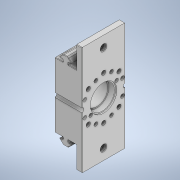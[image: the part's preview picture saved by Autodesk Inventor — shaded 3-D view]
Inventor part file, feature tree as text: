
AUTODESK INVENTOR PART (.ipt)
format: ipt  version: 2020 (Build 240168000, 168)  size: 503,808 bytes
history: native  units: in
note: dims shown in document units (in); Inventor stores cm internally (conversion verified against a paired STEP export)
features: reference x24, extrude x11, sketch x9, other x4, chamfer x2, fillet x1
ambient origin geometry x8: Origin, YZ Plane, XZ Plane, XY Plane, X Axis, Y Axis, Z Axis, Center Point
bodies: Solid1 (feature_tree)
feature tree (51):
  extrude  "Extrusion1"  Depth=5.0in
  extrude  "Extrusion2"  Depth=2.0in TaperAngle=0.0deg
  extrude  "Extrusion4"  Depth=0.5in
  extrude  "Extrusion5"  Depth=0.7874in
  extrude  "Extrusion6"  Depth=2.5in
  extrude  "Extrusion7"  Depth=1.023in
  extrude  "Extrusion8"  Depth=0.314in TaperAngle=0.0deg
  chamfer  "Chamfer3"  Distance=0.064in
  extrude  "Extrusion9"  Depth=0.025in TaperAngle=0.0deg
  extrude  "Extrusion10"  Depth=0.025in
  extrude  "Extrusion11"  Depth=0.025in TaperAngle=0.0deg
  extrude  "Extrusion12"  Depth=0.025in
  fillet  "Fillet1"  Radius=0.165in
  chamfer  "Chamfer4"  [1 undecoded]
  sketch  "Sketch1"  dims[d0=1.25in d1=5.0in]
  reference  "Reference1"
  reference  "Reference2"
  reference  "Reference3"
  reference  "Reference4"
  reference  "Reference5"
  reference  "Reference6"
  reference  "Reference7"
  reference  "Reference8"
  reference  "Reference9"
  reference  "Reference10"
  reference  "Reference11"
  reference  "Reference12"
  reference  "Reference13"
  reference  "Reference14"
  reference  "Reference15"
  reference  "Reference16"
  reference  "Reference17"
  reference  "Reference18"
  reference  "Reference19"
  reference  "Reference20"
  reference  "Reference21"
  reference  "Reference22"
  reference  "Reference23"
  reference  "Reference24"
  sketch  "Sketch2"  dims[d2=0.25in d3=2.0in d4=0.0in]
  sketch  "Sketch4"  dims[d5=0.5in d6=0.5in]
  sketch  "Sketch5"  dims[d7=0.2656in d8=0.7874in d10=4.0in d11=1.1811in d13=0.5in]
  sketch  "Sketch7"  dims[d24=0.0in d25=0.0in d29=2.5in]
  sketch  "Sketch9"  dims[d30=1.0in d31=1.023in]
  sketch  "Sketch10"  dims[d32=1.126in d33=0.314in d34=0.0in]
  sketch  "Sketch11"  dims[d35=1.226in d36=0.064in d37=0.0in]
  sketch  "Sketch12"  dims[d41=1.126in d42=0.314in d43=0.0in d44=1.226in d45=0.064in d46=0.0in d50=1.4291in d51=0.165in d52=0.0in d53=0.0in d54=0.025in d55=0.125in d56=45.0deg d57=1.0in d58=0.196in d59=3.1496in d61=360.0deg d63=0.0in d64=0.0in d65=0.1695in d66=0.9375in d67=22.5deg d68=3.1496in d70=360.0deg d72=0.0in d73=0.0in d74=0.3865in d75=0.125in d76=0.0in d77=0.6in d78=0.6in d79=0.0in d80=0.0in d81=0.0098in d82=0.0098in d83=0.025in d84=0.02in d85=0.125in d86=45.0deg]
  other  "<userpath>\Documents\FRC\2020\ShooterPrototype.iam"
  other  "ShooterPrototype.iam"
  other  "9inSpacer:1"
  other  "1003-48-CL:4"
note: 1 required parameter value undecoded (feature->parameter linkage not recoverable at this tier; creation-order binding heuristic only, values carry confidence <= 0.55)
